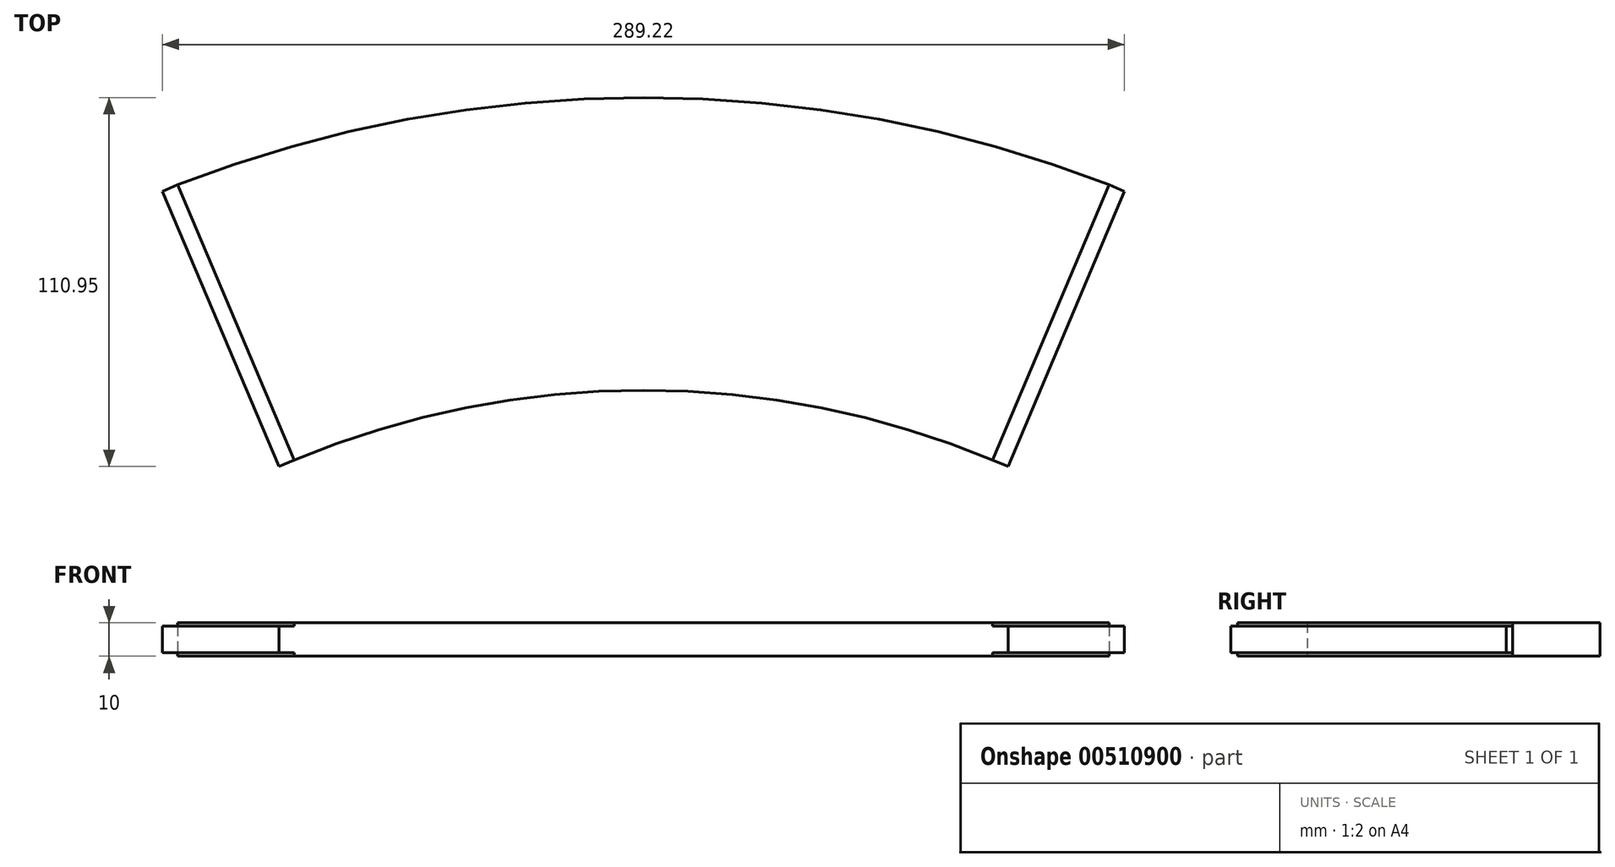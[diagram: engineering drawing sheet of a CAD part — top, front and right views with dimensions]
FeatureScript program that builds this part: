
annotation { "Feature Type Name" : "Feature", "Feature Type Description" : "" }
export const myFeature = defineFeature(function(context is Context, id is Id, definition is map)
    precondition{}
    {
        {
            var Q0;
            Q0=qCreatedBy(makeId("Top.planeOp"),FACE);
            var sketch = newSketch(context, id + "F0", { "sketchPlane" : qUnion([Q0])});
            skLineSegment(sketch, "E0", {"start": v(-140, 0) * mm, "end": v(140, 0) * mm});
            skLineSegment(sketch, "E1", {"start": v(-105, -82.77) * mm, "end": v(105, -82.77) * mm});
            skLineSegment(sketch, "E2", {"start": v(140, 0) * mm, "end": v(105, -82.77) * mm});
            skLineSegment(sketch, "E3", {"start": v(-140, 0) * mm, "end": v(-105, -82.77) * mm});
            skArc(sketch, "E4", {"start": v(140, 0) * mm, "mid": v(0, 26.23) * mm, "end": v(-140, 0) * mm});
            skLineSegment(sketch, "E5.0", {"start": v(-105, -61.77) * mm, "end": v(105, -61.77) * mm});
            skLineSegment(sketch, "E6", {"start": v(0, 26.23) * mm, "end": v(0, -82.77) * mm});
            skArc(sketch, "E7", {"start": v(105, -82.77) * mm, "mid": v(0, -61.77) * mm, "end": v(-105, -82.77) * mm});
            skPoint(sketch, "E8.orphan", {"position": v(0, -61.77) * mm});
            skSolve(sketch);
        }
        {
            var Q0;
            Q0=makeQuery(id+"F0.imprint","IMPRINT",FACE,{"disambiguationData":[TD([[makeQuery(id+"F0.imprint","IMPRINT",EDGE,{"derivedFrom":sQuery(id+"F0.wireOp",EDGE,"E0")}),-1.0]])]});
            var Q1;
            Q1=makeQuery(id+"F0.imprint","IMPRINT",FACE,{"disambiguationData":[TD([[makeQuery(id+"F0.imprint","IMPRINT",EDGE,{"derivedFrom":sQuery(id+"F0.wireOp",EDGE,"E0")}),1.0]])]});
            extrude(context, id + "F1", {"entities" : qUnion([Q0, Q1]), "depth" : 10 * mm});
        }
        {
            var Q0;
            Q0=makeQuery(id+"F1.opExtrude","SWEPT_FACE",FACE,{"disambiguationData":[OSD([sQuery(id+"F0.wireOp",EDGE,"E2")])]});
            var sketch = newSketch(context, id + "F2", { "sketchPlane" : qUnion([Q0])});
            skLineSegment(sketch, "E9.0.0", {"start": v(-35.34, 0) * mm, "end": v(54.52, 0) * mm});
            skLineSegment(sketch, "E9.0.1", {"start": v(54.52, 0) * mm, "end": v(54.52, 10) * mm});
            skLineSegment(sketch, "E9.0.2", {"start": v(54.52, 10) * mm, "end": v(-35.34, 10) * mm});
            skLineSegment(sketch, "E9.0.3", {"start": v(-35.34, 10) * mm, "end": v(-35.34, 0) * mm});
            skLineSegment(sketch, "E10.1", {"start": v(-35.34, 1) * mm, "end": v(54.52, 1) * mm});
            skLineSegment(sketch, "E10.3", {"start": v(54.52, 9) * mm, "end": v(-35.34, 9) * mm});
            skSolve(sketch);
        }
        {
            var Q0;
            Q0=makeQuery(id+"F2.imprint","IMPRINT",FACE,{"disambiguationData":[TD([[makeQuery(id+"F2.imprint","IMPRINT",EDGE,{"derivedFrom":sQuery(id+"F2.wireOp",EDGE,"E10.0")}),1.0]])]});
            var Q1;
            {var subQ0=sQuery(id+"F2.wireOp",EDGE,"E10.1");Q1=makeQuery(id+"F2.imprint","IMPRINT",FACE,{"disambiguationData":[TD([[makeQuery(id+"F2.imprint","IMPRINT",EDGE,{"derivedFrom":subQ0}),1.0]])]});}
            extrude(context, id + "F3", {"entities" : qUnion([Q0, Q1]), "operationType" : NewBodyOperationType.ADD, "depth" : 5 * mm});
        }
        {
            var Q0;
            Q0=makeQuery(id+"F1.opExtrude","SWEPT_FACE",FACE,{"disambiguationData":[OSD([sQuery(id+"F0.wireOp",EDGE,"E3")])]});
            var sketch = newSketch(context, id + "F4", { "sketchPlane" : qUnion([Q0])});
            skLineSegment(sketch, "E11.0.0", {"start": v(-54.52, 0) * mm, "end": v(35.34, 0) * mm});
            skLineSegment(sketch, "E11.0.1", {"start": v(35.34, 0) * mm, "end": v(35.34, 10) * mm});
            skLineSegment(sketch, "E11.0.2", {"start": v(35.34, 10) * mm, "end": v(-54.52, 10) * mm});
            skLineSegment(sketch, "E11.0.3", {"start": v(-54.52, 10) * mm, "end": v(-54.52, 0) * mm});
            skLineSegment(sketch, "E12.0", {"start": v(-54.52, 1) * mm, "end": v(35.34, 1) * mm});
            skLineSegment(sketch, "E12.2", {"start": v(35.34, 9) * mm, "end": v(-54.52, 9) * mm});
            skSolve(sketch);
        }
        {
            var Q0;
            Q0=makeQuery(id+"F4.imprint","IMPRINT",FACE,{"disambiguationData":[TD([[makeQuery(id+"F4.imprint","IMPRINT",EDGE,{"derivedFrom":sQuery(id+"F4.wireOp",EDGE,"E12.0")}),1.0]])]});
            extrude(context, id + "F5", {"entities" : qUnion([Q0]), "operationType" : NewBodyOperationType.ADD, "depth" : 5 * mm});
        }
    });
